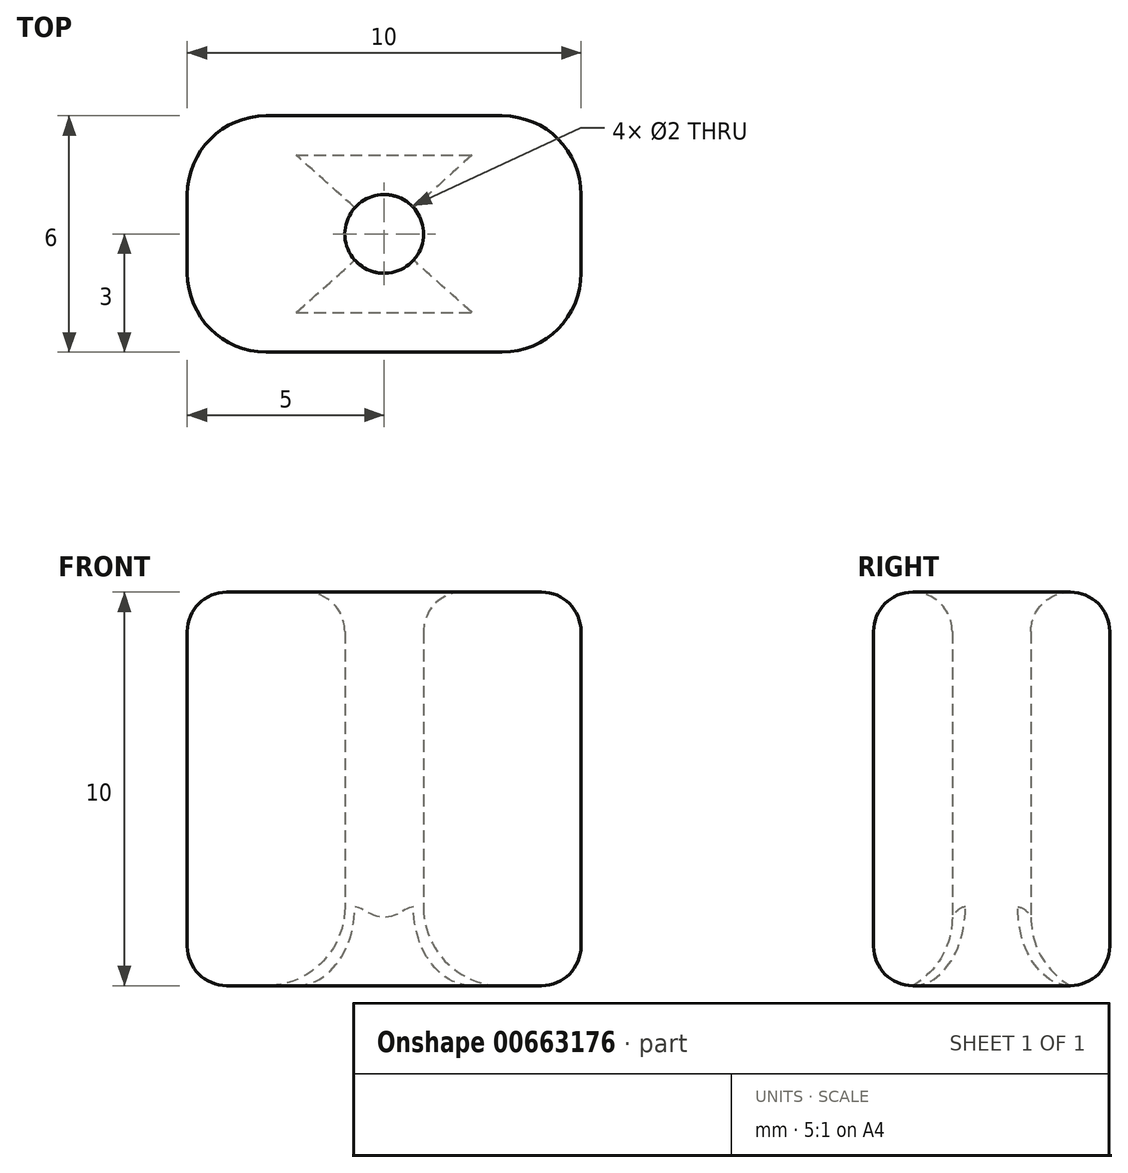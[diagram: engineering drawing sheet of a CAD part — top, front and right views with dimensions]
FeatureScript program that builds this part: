
annotation { "Feature Type Name" : "Feature", "Feature Type Description" : "" }
export const myFeature = defineFeature(function(context is Context, id is Id, definition is map)
    precondition{}
    {
        {
            var Q0;
            Q0=qCreatedBy(makeId("Top.planeOp"),FACE);
            var sketch = newSketch(context, id + "F0", { "sketchPlane" : qUnion([Q0])});
            skLineSegment(sketch, "E0.bottom", {"start": v(-10, 6) * mm, "end": v(0, 6) * mm});
            skLineSegment(sketch, "E0.top", {"start": v(-10, 0) * mm, "end": v(0, 0) * mm});
            skLineSegment(sketch, "E0.left", {"start": v(-10, 6) * mm, "end": v(-10, 0) * mm});
            skLineSegment(sketch, "E0.right", {"start": v(0, 6) * mm, "end": v(0, 0) * mm});
            skLineSegment(sketch, "E1", {"start": v(-5, 6) * mm, "end": v(-5, 0) * mm, "construction": true});
            skLineSegment(sketch, "E2", {"start": v(-10, 3) * mm, "end": v(0, 3) * mm, "construction": true});
            skCircle(sketch, "E3", {"center": v(-5, 3) * mm, "radius": 1 * mm});
            skSolve(sketch);
        }
        {
            var Q0;
            Q0=makeQuery(id+"F0.imprint","IMPRINT",FACE,{"disambiguationData":[TD([[makeQuery(id+"F0.imprint","IMPRINT",EDGE,{"derivedFrom":sQuery(id+"F0.wireOp",EDGE,"E0.bottom")}),-1.0]])]});
            extrude(context, id + "F1", {"entities" : qUnion([Q0]), "depth" : 10 * mm, "offsetDistance" : 25 * mm});
        }
        {
            var Q0;
            Q0=makeQuery(id+"F1.opExtrude","CAP_EDGE",EDGE,{"disambiguationData":[OSD([sQuery(id+"F0.wireOp",EDGE,"E0.left")])],"isStart":false});
            var Q1;
            Q1=makeQuery(id+"F1.opExtrude","CAP_EDGE",EDGE,{"disambiguationData":[OSD([sQuery(id+"F0.wireOp",EDGE,"E0.bottom")])],"isStart":false});
            var Q2;
            Q2=makeQuery(id+"F1.opExtrude","CAP_EDGE",EDGE,{"disambiguationData":[OSD([sQuery(id+"F0.wireOp",EDGE,"E0.top")])],"isStart":false});
            var Q3;
            Q3=makeQuery(id+"F1.opExtrude","CAP_EDGE",EDGE,{"disambiguationData":[OSD([sQuery(id+"F0.wireOp",EDGE,"E0.right")])],"isStart":false});
            var Q4;
            Q4=makeQuery(id+"F1.opExtrude","CAP_EDGE",EDGE,{"disambiguationData":[OSD([sQuery(id+"F0.wireOp",EDGE,"E0.right")])],"isStart":true});
            var Q5;
            Q5=makeQuery(id+"F1.opExtrude","CAP_EDGE",EDGE,{"disambiguationData":[OSD([sQuery(id+"F0.wireOp",EDGE,"E0.bottom")])],"isStart":true});
            var Q6;
            Q6=makeQuery(id+"F1.opExtrude","CAP_EDGE",EDGE,{"disambiguationData":[OSD([sQuery(id+"F0.wireOp",EDGE,"E0.left")])],"isStart":true});
            var Q7;
            Q7=makeQuery(id+"F1.opExtrude","CAP_EDGE",EDGE,{"disambiguationData":[OSD([sQuery(id+"F0.wireOp",EDGE,"E0.top")])],"isStart":true});
            fillet(context, id + "F2", {"entities" : qUnion([Q0, Q1, Q2, Q3, Q4, Q5, Q6, Q7]), "radius" : 1 * mm, "tangentPropagation" : true, "allowEdgeOverflow" : false});
        }
        {
            var Q0;
            Q0=makeQuery(id+"F1.opExtrude","CAP_EDGE",EDGE,{"disambiguationData":[OSD([sQuery(id+"F0.wireOp",EDGE,"E3")])],"isStart":true});
            fillet(context, id + "F3", {"entities" : qUnion([Q0]), "radius" : 2 * mm, "tangentPropagation" : true, "allowEdgeOverflow" : false});
        }
        {
            var Q0;
            Q0=makeQuery(id+"F1.opExtrude","SWEPT_EDGE",EDGE,{"disambiguationData":[OSD([sQuery(id+"F0.wireOp",EDGE,"E0.top"),sQuery(id+"F0.wireOp",EDGE,"E0.right")])]});
            var Q1;
            Q1=makeQuery(id+"F1.opExtrude","SWEPT_EDGE",EDGE,{"disambiguationData":[OSD([sQuery(id+"F0.wireOp",EDGE,"E0.top"),sQuery(id+"F0.wireOp",EDGE,"E0.left")])]});
            var Q2;
            Q2=makeQuery(id+"F1.opExtrude","SWEPT_EDGE",EDGE,{"disambiguationData":[OSD([sQuery(id+"F0.wireOp",EDGE,"E0.bottom"),sQuery(id+"F0.wireOp",EDGE,"E0.left")])]});
            var Q3;
            Q3=makeQuery(id+"F1.opExtrude","SWEPT_EDGE",EDGE,{"disambiguationData":[OSD([sQuery(id+"F0.wireOp",EDGE,"E0.bottom"),sQuery(id+"F0.wireOp",EDGE,"E0.right")])]});
            fillet(context, id + "F4", {"entities" : qUnion([Q0, Q1, Q2, Q3]), "radius" : 2 * mm, "tangentPropagation" : true, "allowEdgeOverflow" : false});
        }
        {
            var Q0;
            Q0=makeQuery(id+"F1.opExtrude","CAP_EDGE",EDGE,{"disambiguationData":[OSD([sQuery(id+"F0.wireOp",EDGE,"E3")])],"isStart":false});
            fillet(context, id + "F5", {"entities" : qUnion([Q0]), "radius" : 1 * mm, "tangentPropagation" : true, "allowEdgeOverflow" : false});
        }
    });
